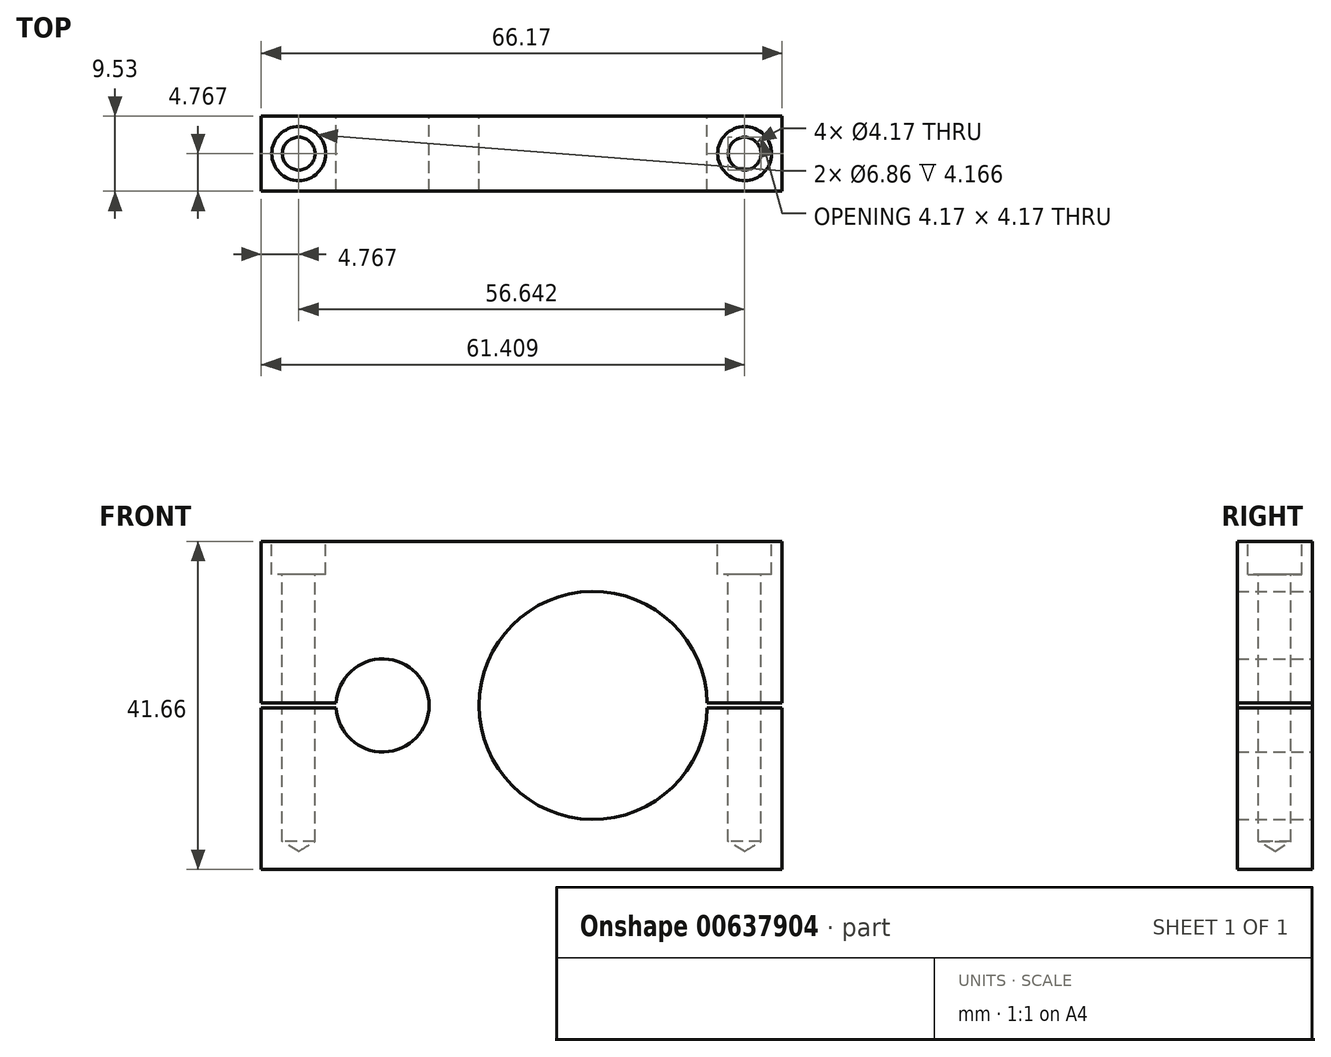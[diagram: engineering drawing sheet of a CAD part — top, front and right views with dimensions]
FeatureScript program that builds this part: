
annotation { "Feature Type Name" : "Feature", "Feature Type Description" : "" }
export const myFeature = defineFeature(function(context is Context, id is Id, definition is map)
    precondition{}
    {
        {
            var Q0;
            Q0=qCreatedBy(makeId("Front.planeOp"),FACE);
            var sketch = newSketch(context, id + "F0", { "sketchPlane" : qUnion([Q0])});
            skPoint(sketch, "E0", {"position": v(-6.77, 0) * mm});
            skPoint(sketch, "E1", {"position": v(19.97, 0) * mm});
            skCircle(sketch, "E2", {"center": v(-6.77, 0) * mm, "radius": 5.9 * mm});
            skCircle(sketch, "E3", {"center": v(19.97, 0) * mm, "radius": 14.48 * mm});
            skLineSegment(sketch, "E4.bottom", {"start": v(-22.2, 20.83) * mm, "end": v(43.97, 20.83) * mm});
            skLineSegment(sketch, "E4.top", {"start": v(-22.2, -20.83) * mm, "end": v(43.97, -20.83) * mm});
            skLineSegment(sketch, "E4.left", {"start": v(-22.2, 20.83) * mm, "end": v(-22.2, -20.83) * mm});
            skLineSegment(sketch, "E4.right", {"start": v(43.97, 20.83) * mm, "end": v(43.97, -20.83) * mm});
            skLineSegment(sketch, "E5", {"start": v(-22.2, 0) * mm, "end": v(43.97, 0) * mm, "construction": true});
            skPoint(sketch, "E6", {"position": v(43.97, 0.32) * mm});
            skLineSegment(sketch, "E7", {"start": v(43.97, 0.32) * mm, "end": v(34.44, 0.32) * mm});
            skLineSegment(sketch, "E8.MirrorCS", {"start": v(43.97, -0.32) * mm, "end": v(34.44, -0.32) * mm});
            skPoint(sketch, "E9", {"position": v(-22.2, 0.32) * mm});
            skLineSegment(sketch, "E10", {"start": v(-22.2, 0.32) * mm, "end": v(-12.66, 0.32) * mm});
            skLineSegment(sketch, "E11.MirrorCS", {"start": v(-22.2, -0.32) * mm, "end": v(-12.66, -0.32) * mm});
            skSolve(sketch);
        }
        {
            var Q0;
            {var subQ3=sQuery(id+"F0.wireOp",EDGE,"E4.bottom");Q0=makeQuery(id+"F0.imprint","IMPRINT",FACE,{"disambiguationData":[TD([[makeQuery(id+"F0.imprint","IMPRINT",EDGE,{"derivedFrom":subQ3}),-1.0]])]});}
            extrude(context, id + "F1", {"entities" : qUnion([Q0]), "depth" : 9.52 * mm, "offsetDistance" : 25.4 * mm});
        }
        {
            var Q0;
            Q0=makeQuery(id+"F1.opExtrude","SWEPT_FACE",FACE,{"disambiguationData":[OSD([sQuery(id+"F0.wireOp",EDGE,"E4.bottom")])]});
            var sketch = newSketch(context, id + "F2", { "sketchPlane" : qUnion([Q0])});
            skPoint(sketch, "E12", {"position": v(39.2, -4.76) * mm});
            skPoint(sketch, "E12.positionSnap0", {"position": v(43.97, -4.76) * mm});
            skLineSegment(sketch, "E13", {"start": v(0, 0) * mm, "end": v(0, -9.53) * mm, "construction": true});
            skPoint(sketch, "E14", {"position": v(-17.43, -4.76) * mm});
            skPoint(sketch, "E14.positionSnap0", {"position": v(-22.2, -4.76) * mm});
            skSolve(sketch);
        }
        {
            var Q0;
            Q0=sQuery(id+"F2.wireOp",VERTEX,"E14");
            var Q1;
            Q1=sQuery(id+"F2.wireOp",VERTEX,"E12");
            var Q2;
            Q2=makeQuery(id+"F1.opExtrude","SWEPT_BODY",BODY,{"disambiguationData":[OSD([sQuery(id+"F0.wireOp",EDGE,"E2"),sQuery(id+"F0.wireOp",EDGE,"E3"),sQuery(id+"F0.wireOp",EDGE,"E4.bottom"),sQuery(id+"F0.wireOp",EDGE,"E4.top"),sQuery(id+"F0.wireOp",EDGE,"E4.left"),sQuery(id+"F0.wireOp",EDGE,"E4.right"),sQuery(id+"F0.wireOp",EDGE,"E7"),sQuery(id+"F0.wireOp",EDGE,"E8.MirrorCS"),sQuery(id+"F0.wireOp",EDGE,"E10"),sQuery(id+"F0.wireOp",EDGE,"E11.MirrorCS")])]});
            hole(context, id + "F3", {"style" : HoleStyle.C_BORE, "endStyle" : HoleEndStyle.BLIND, "holeDiameter" : 4.17 * mm, "cBoreDiameter" : 6.86 * mm, "cBoreDepth" : 4.17 * mm, "majorDiameter" : 6.35 * mm, "holeDepth" : 38.1 * mm, "isTappedThrough" : true, "tappedDepth" : 12.7 * mm, "tapClearance" : 3, "locations" : qUnion([Q0, Q1]), "scope" : qUnion([Q2])});
        }
    });
